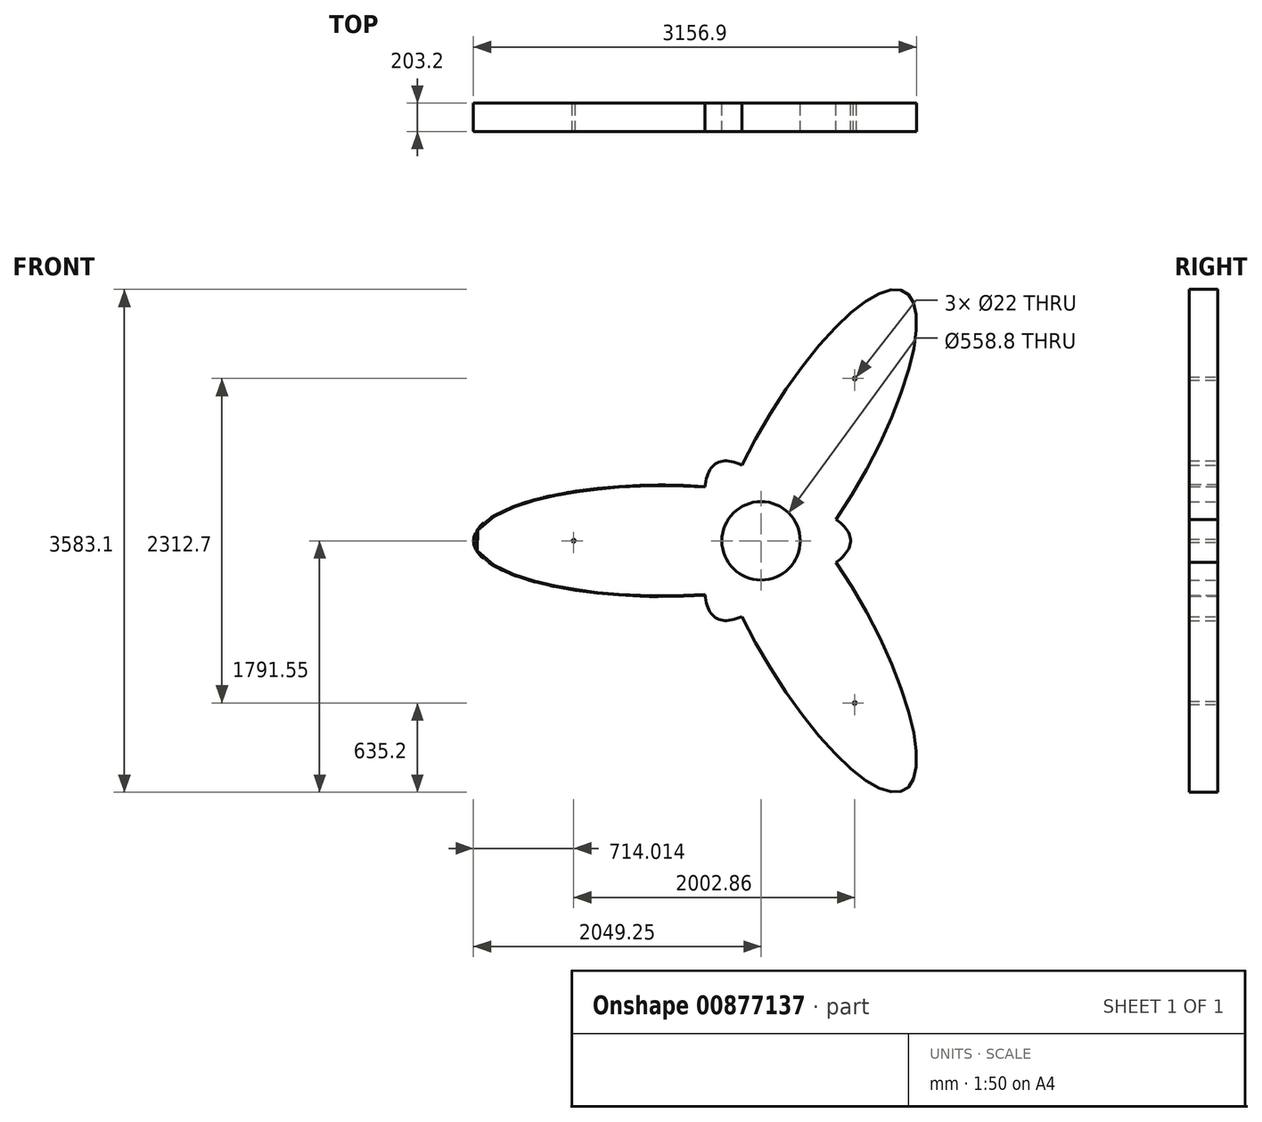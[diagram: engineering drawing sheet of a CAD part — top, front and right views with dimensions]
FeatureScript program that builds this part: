
annotation { "Feature Type Name" : "Feature", "Feature Type Description" : "" }
export const myFeature = defineFeature(function(context is Context, id is Id, definition is map)
    precondition{}
    {
        {
            var Q0;
            Q0=qCreatedBy(makeId("Front.planeOp"),FACE);
            var sketch = newSketch(context, id + "F0", { "sketchPlane" : qUnion([Q0])});
            skEllipse(sketch, "E0", {"center": v(-97.66, 38.07) * mm, "majorRadius": 1343.4 * mm, "minorRadius": 397.39 * mm, "majorAxis": v(1, 0)});
            skCircle(sketch, "E1", {"center": v(608.18, 38.07) * mm, "radius": 279.4 * mm});
            skCircle(sketch, "E2", {"center": v(-727.06, 38.07) * mm, "radius": 11 * mm});
            skCircle(sketch, "E3.1.0", {"center": v(1275.8, -1118.28) * mm, "radius": 11 * mm});
            skEllipse(sketch, "E3.1.2", {"center": v(961.1, -573.2) * mm, "majorRadius": 1343.4 * mm, "minorRadius": 397.39 * mm, "majorAxis": v(-0.5, 0.87)});
            skCircle(sketch, "E3.2.0", {"center": v(1275.8, 1194.42) * mm, "radius": 11 * mm});
            skEllipse(sketch, "E3.2.2", {"center": v(961.1, 649.35) * mm, "majorRadius": 1343.4 * mm, "minorRadius": 397.39 * mm, "majorAxis": v(-0.5, -0.87)});
            skSolve(sketch);
        }
        {
            var Q0;
            Q0 = qSketchRegion(id + "F0", true);
            var Q1;
            Q1=makeQuery(id+"F0.imprint","IMPRINT",FACE,{"disambiguationData":[TD([[makeQuery(id+"F0.imprint","IMPRINT",EDGE,{"derivedFrom":sQuery(id+"F0.wireOp",EDGE,"E1")}),-1.0]])]});
            extrude(context, id + "F1", {"entities" : qUnion([Q0, Q1]), "depth" : 203.2 * mm, "offsetDistance" : 25.4 * mm});
        }
        {
            var Q0;
            {var subQ0=sQuery(id+"F0.wireOp",EDGE,"E0");Q0=makeQuery(id+"F1.opExtrude","CAP_EDGE",EDGE,{"disambiguationData":[OSD([subQ0]),TDD([makeQuery(id+"F0.imprint","IMPRINT",EDGE,{"disambiguationData":[TD([[makeQuery(id+"F0.imprint","INTERSECT",VERTEX,{"disambiguationData":[OD(0.0)],"derivedFrom":[subQ0,sQuery(id+"F0.wireOp",EDGE,"E3.1.2")]}),-1.0]])],"derivedFrom":subQ0})])],"isStart":false});}
            fillet(context, id + "F2", {"entities" : qUnion([Q0]), "radius" : 5.08 * mm, "tangentPropagation" : true, "allowEdgeOverflow" : false});
        }
    });
